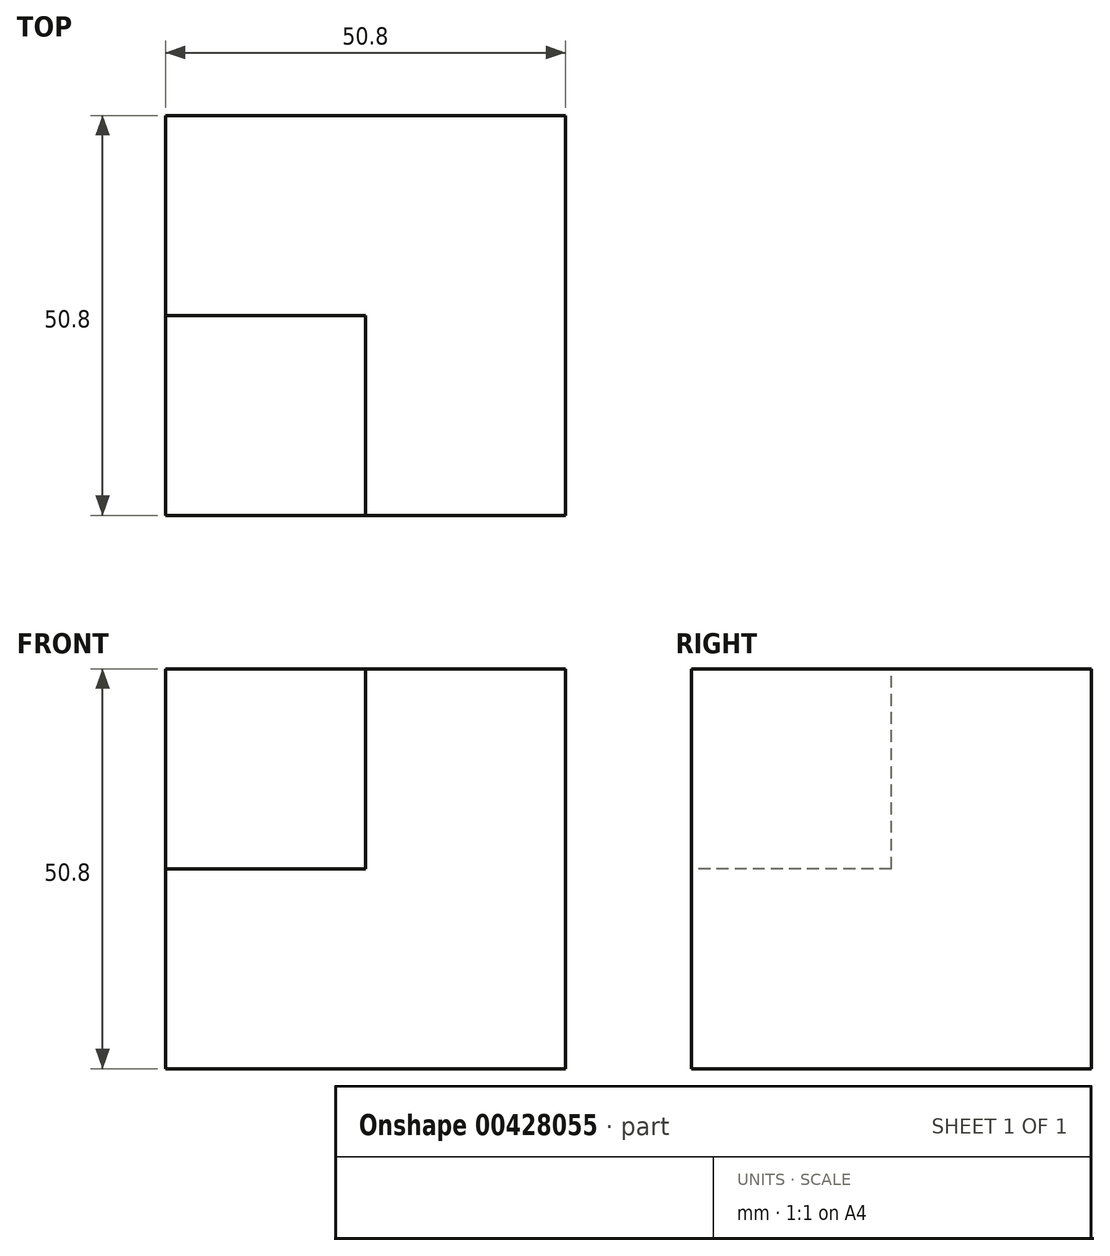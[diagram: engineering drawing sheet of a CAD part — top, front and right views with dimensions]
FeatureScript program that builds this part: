
annotation { "Feature Type Name" : "Feature", "Feature Type Description" : "" }
export const myFeature = defineFeature(function(context is Context, id is Id, definition is map)
    precondition{}
    {
        {
            var Q0;
            Q0=qCreatedBy(makeId("Front.planeOp"),FACE);
            var sketch = newSketch(context, id + "F0", { "sketchPlane" : qUnion([Q0])});
            skLineSegment(sketch, "E0", {"start": v(0, 0) * mm, "end": v(-50.8, 0) * mm});
            skLineSegment(sketch, "E1", {"start": v(-50.8, 0) * mm, "end": v(-50.8, 50.8) * mm});
            skLineSegment(sketch, "E2", {"start": v(-50.8, 50.8) * mm, "end": v(0, 50.8) * mm});
            skLineSegment(sketch, "E3", {"start": v(0, 50.8) * mm, "end": v(0, 0) * mm});
            skSolve(sketch);
        }
        {
            var Q0;
            Q0 = qSketchRegion(id + "F0", true);
            extrude(context, id + "F1", {"entities" : qUnion([Q0]), "depth" : 50.8 * mm});
        }
        {
            var Q0;
            Q0=makeQuery(id+"F1.opExtrude","CAP_FACE",FACE,{"disambiguationData":[OSD([sQuery(id+"F0.wireOp",EDGE,"E0"),sQuery(id+"F0.wireOp",EDGE,"E1"),sQuery(id+"F0.wireOp",EDGE,"E2"),sQuery(id+"F0.wireOp",EDGE,"E3")])],"isStart":false});
            var sketch = newSketch(context, id + "F2", { "sketchPlane" : qUnion([Q0])});
            skLineSegment(sketch, "E4", {"start": v(-50.8, 50.8) * mm, "end": v(-25.4, 50.8) * mm});
            skLineSegment(sketch, "E5", {"start": v(-25.4, 50.8) * mm, "end": v(-25.4, 25.4) * mm});
            skPoint(sketch, "E5.endSnap0", {"position": v(0, 25.4) * mm});
            skLineSegment(sketch, "E6", {"start": v(-25.4, 25.4) * mm, "end": v(-50.8, 25.4) * mm});
            skLineSegment(sketch, "E7", {"start": v(-50.8, 25.4) * mm, "end": v(-50.8, 50.8) * mm});
            skSolve(sketch);
        }
        {
            var Q0;
            Q0 = qSketchRegion(id + "F2", true);
            extrude(context, id + "F3", {"entities" : qUnion([Q0]), "operationType" : NewBodyOperationType.REMOVE, "oppositeDirection" : true, "depth" : 25.4 * mm});
        }
    });
